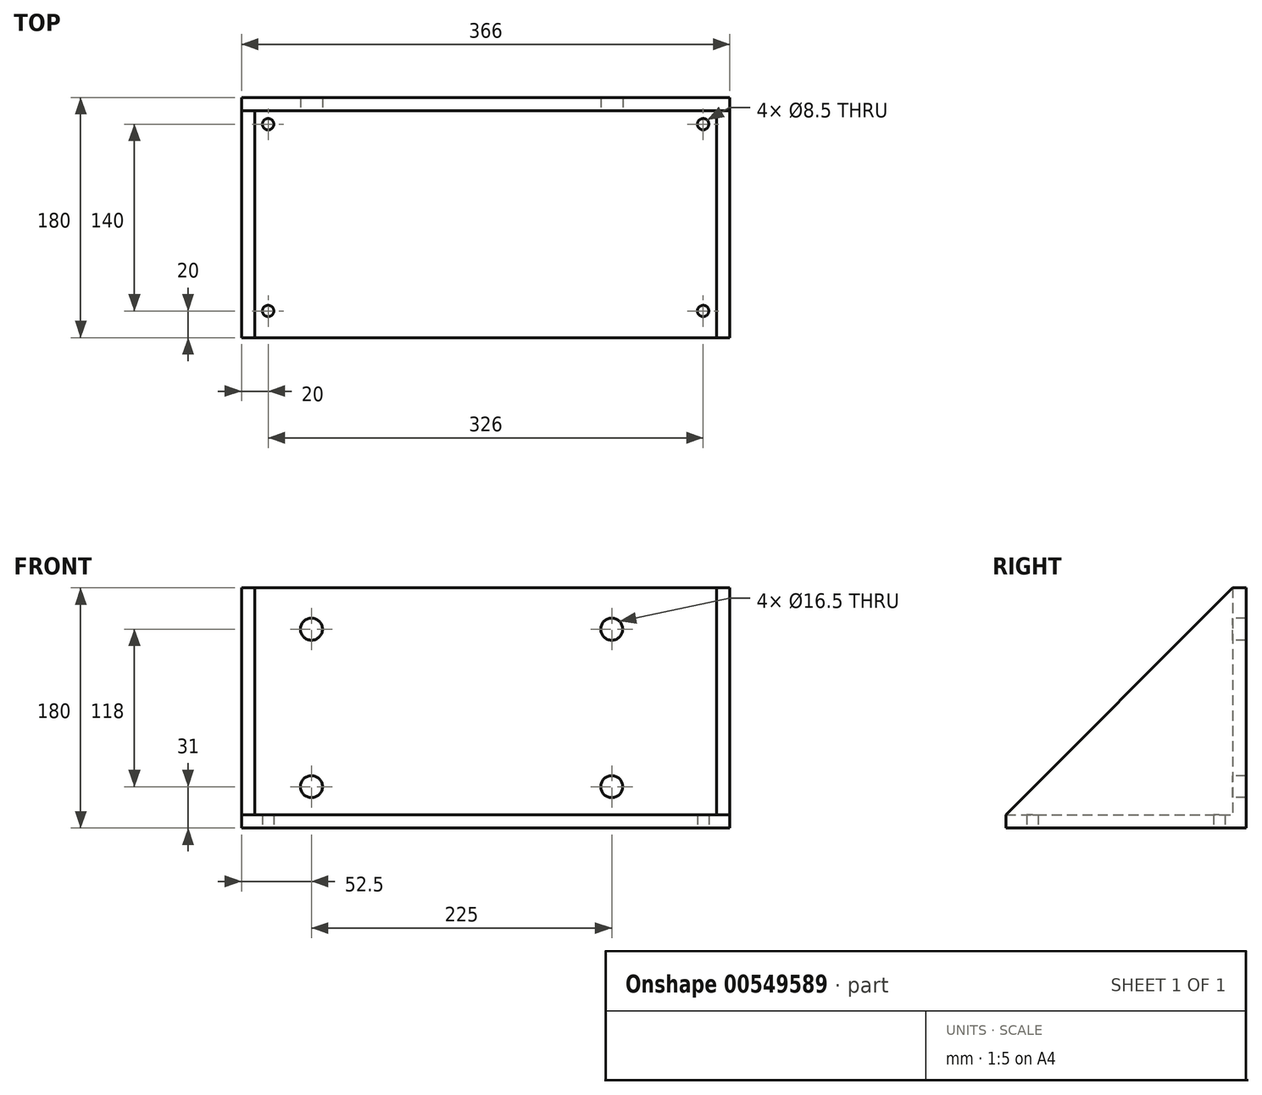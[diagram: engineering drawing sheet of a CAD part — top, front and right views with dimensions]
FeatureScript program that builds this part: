
annotation { "Feature Type Name" : "Feature", "Feature Type Description" : "" }
export const myFeature = defineFeature(function(context is Context, id is Id, definition is map)
    precondition{}
    {
        {
            var Q0;
            Q0=qCreatedBy(makeId("Right.planeOp"),FACE);
            var sketch = newSketch(context, id + "F0", { "sketchPlane" : qUnion([Q0])});
            skLineSegment(sketch, "E0", {"start": v(10, 85) * mm, "end": v(10, -95) * mm});
            skLineSegment(sketch, "E1", {"start": v(10, -95) * mm, "end": v(-170, -95) * mm});
            skLineSegment(sketch, "E2", {"start": v(-170, -95) * mm, "end": v(-170, -85) * mm});
            skLineSegment(sketch, "E3", {"start": v(-170, -85) * mm, "end": v(0, -85) * mm});
            skLineSegment(sketch, "E4", {"start": v(0, -85) * mm, "end": v(0, 85) * mm});
            skLineSegment(sketch, "E5", {"start": v(0, 85) * mm, "end": v(10, 85) * mm});
            skSolve(sketch);
        }
        {
            var Q0;
            Q0=makeQuery(id+"F0.imprint","IMPRINT",FACE,{"disambiguationData":[TD([[makeQuery(id+"F0.imprint","IMPRINT",EDGE,{"derivedFrom":sQuery(id+"F0.wireOp",EDGE,"E0")}),-1.0]])]});
            extrude(context, id + "F1", {"entities" : qUnion([Q0]), "depth" : 366 * mm, "offsetDistance" : 25 * mm});
        }
        {
            var Q0;
            Q0=makeQuery(id+"F1.opExtrude","SWEPT_FACE",FACE,{"disambiguationData":[OSD([sQuery(id+"F0.wireOp",EDGE,"E4")])]});
            var sketch = newSketch(context, id + "F2", { "sketchPlane" : qUnion([Q0])});
            skLineSegment(sketch, "E6", {"start": v(-34.72, 54) * mm, "end": v(411.3, 54) * mm, "construction": true});
            skLineSegment(sketch, "E7", {"start": v(-33.79, -64) * mm, "end": v(425.27, -64) * mm, "construction": true});
            skLineSegment(sketch, "E8", {"start": v(52.5, 122.85) * mm, "end": v(52.5, -132.75) * mm, "construction": true});
            skLineSegment(sketch, "E9", {"start": v(277.5, 121.45) * mm, "end": v(277.5, -137.87) * mm, "construction": true});
            skCircle(sketch, "E10", {"center": v(52.5, 54) * mm, "radius": 8.25 * mm});
            skCircle(sketch, "E11", {"center": v(277.5, -64) * mm, "radius": 8.25 * mm});
            skCircle(sketch, "E12", {"center": v(277.5, 54) * mm, "radius": 8.25 * mm});
            skCircle(sketch, "E13", {"center": v(52.5, -64) * mm, "radius": 8.25 * mm});
            skSolve(sketch);
        }
        {
            var Q0;
            Q0=makeQuery(id+"F2.imprint","IMPRINT",FACE,{"disambiguationData":[TD([[makeQuery(id+"F2.imprint","IMPRINT",EDGE,{"derivedFrom":sQuery(id+"F2.wireOp",EDGE,"E10")}),1.0]])]});
            var Q1;
            Q1=makeQuery(id+"F2.imprint","IMPRINT",FACE,{"disambiguationData":[TD([[makeQuery(id+"F2.imprint","IMPRINT",EDGE,{"derivedFrom":sQuery(id+"F2.wireOp",EDGE,"E12")}),1.0]])]});
            var Q2;
            Q2=makeQuery(id+"F2.imprint","IMPRINT",FACE,{"disambiguationData":[TD([[makeQuery(id+"F2.imprint","IMPRINT",EDGE,{"derivedFrom":sQuery(id+"F2.wireOp",EDGE,"E11")}),1.0]])]});
            var Q3;
            Q3=makeQuery(id+"F2.imprint","IMPRINT",FACE,{"disambiguationData":[TD([[makeQuery(id+"F2.imprint","IMPRINT",EDGE,{"derivedFrom":sQuery(id+"F2.wireOp",EDGE,"E13")}),1.0]])]});
            extrude(context, id + "F3", {"entities" : qUnion([Q0, Q1, Q2, Q3]), "operationType" : NewBodyOperationType.REMOVE, "endBound" : BoundingType.THROUGH_ALL, "oppositeDirection" : true, "depth" : 25 * mm, "offsetDistance" : 25 * mm});
        }
        {
            var Q0;
            Q0=makeQuery(id+"F1.opExtrude","SWEPT_FACE",FACE,{"disambiguationData":[OSD([sQuery(id+"F0.wireOp",EDGE,"E4")])]});
            var sketch = newSketch(context, id + "F4", { "sketchPlane" : qUnion([Q0])});
            skLineSegment(sketch, "E14.bottom", {"start": v(366, 85) * mm, "end": v(356, 85) * mm});
            skLineSegment(sketch, "E14.top", {"start": v(366, -85) * mm, "end": v(356, -85) * mm});
            skLineSegment(sketch, "E14.left", {"start": v(366, 85) * mm, "end": v(366, -85) * mm});
            skLineSegment(sketch, "E14.right", {"start": v(356, 85) * mm, "end": v(356, -85) * mm});
            skLineSegment(sketch, "E15.bottom", {"start": v(0, 85) * mm, "end": v(10, 85) * mm});
            skLineSegment(sketch, "E15.top", {"start": v(0, -85) * mm, "end": v(10, -85) * mm});
            skLineSegment(sketch, "E15.left", {"start": v(0, 85) * mm, "end": v(0, -85) * mm});
            skLineSegment(sketch, "E15.right", {"start": v(10, 85) * mm, "end": v(10, -85) * mm});
            skSolve(sketch);
        }
        {
            var Q0;
            Q0=makeQuery(id+"F4.imprint","IMPRINT",FACE,{"disambiguationData":[TD([[makeQuery(id+"F4.imprint","IMPRINT",EDGE,{"derivedFrom":sQuery(id+"F4.wireOp",EDGE,"E15.bottom")}),1.0]])]});
            var Q1;
            Q1=makeQuery(id+"F4.imprint","IMPRINT",FACE,{"disambiguationData":[TD([[makeQuery(id+"F4.imprint","IMPRINT",EDGE,{"derivedFrom":sQuery(id+"F4.wireOp",EDGE,"E14.bottom")}),1.0]])]});
            extrude(context, id + "F5", {"entities" : qUnion([Q0, Q1]), "operationType" : NewBodyOperationType.ADD, "depth" : 170 * mm, "offsetDistance" : 25 * mm});
        }
        {
            var Q0;
            Q0=makeQuery(id+"F5.boolean.opBoolean","MERGE",FACE,{"derivedFrom":[makeQuery(id+"F1.opExtrude","CAP_FACE",FACE,{"disambiguationData":[OSD([sQuery(id+"F0.wireOp",EDGE,"E0"),sQuery(id+"F0.wireOp",EDGE,"E1"),sQuery(id+"F0.wireOp",EDGE,"E2"),sQuery(id+"F0.wireOp",EDGE,"E3"),sQuery(id+"F0.wireOp",EDGE,"E4"),sQuery(id+"F0.wireOp",EDGE,"E5")])],"isStart":false}),makeQuery(id+"F5.opExtrude","SWEPT_FACE",FACE,{"disambiguationData":[OSD([sQuery(id+"F4.wireOp",EDGE,"E14.left")])]})]});
            var sketch = newSketch(context, id + "F6", { "sketchPlane" : qUnion([Q0])});
            skLineSegment(sketch, "E16", {"start": v(-225.43, -85) * mm, "end": v(49.68, -85) * mm, "construction": true});
            skLineSegment(sketch, "E17", {"start": v(5, 97.23) * mm, "end": v(5, -95) * mm, "construction": true});
            skLineSegment(sketch, "E18", {"start": v(5, 85) * mm, "end": v(-170, -85) * mm});
            skSolve(sketch);
        }
        {
            var Q0;
            Q0=makeQuery(id+"F5.boolean.opBoolean","MERGE",FACE,{"derivedFrom":[makeQuery(id+"F1.opExtrude","CAP_FACE",FACE,{"disambiguationData":[OSD([sQuery(id+"F0.wireOp",EDGE,"E0"),sQuery(id+"F0.wireOp",EDGE,"E1"),sQuery(id+"F0.wireOp",EDGE,"E2"),sQuery(id+"F0.wireOp",EDGE,"E3"),sQuery(id+"F0.wireOp",EDGE,"E4"),sQuery(id+"F0.wireOp",EDGE,"E5")])],"isStart":true}),makeQuery(id+"F5.opExtrude","SWEPT_FACE",FACE,{"disambiguationData":[OSD([sQuery(id+"F4.wireOp",EDGE,"E15.left")])]})]});
            var sketch = newSketch(context, id + "F7", { "sketchPlane" : qUnion([Q0])});
            skLineSegment(sketch, "E19", {"start": v(-23.48, -85) * mm, "end": v(187.5, -85) * mm, "construction": true});
            skLineSegment(sketch, "E20", {"start": v(0, 160.14) * mm, "end": v(0, -178.78) * mm, "construction": true});
            skLineSegment(sketch, "E21", {"start": v(0, 85) * mm, "end": v(170, -85) * mm});
            skSolve(sketch);
        }
        {
            var Q0;
            {var subQ0=sQuery(id+"F7.wireOp",EDGE,"E21");Q0=makeQuery(id+"F7.imprint","IMPRINT",FACE,{"disambiguationData":[TD([[makeQuery(id+"F7.imprint","IMPRINT",EDGE,{"derivedFrom":subQ0}),1.0]])]});}
            var Q1;
            {var subQ0=sQuery(id+"F6.wireOp",EDGE,"E18");Q1=makeQuery(id+"F6.imprint","IMPRINT",FACE,{"disambiguationData":[TD([[makeQuery(id+"F6.imprint","IMPRINT",EDGE,{"derivedFrom":subQ0}),-1.0]])]});}
            extrude(context, id + "F8", {"entities" : qUnion([Q0, Q1]), "operationType" : NewBodyOperationType.REMOVE, "endBound" : BoundingType.THROUGH_ALL, "oppositeDirection" : true, "depth" : 25 * mm, "offsetDistance" : 25 * mm});
        }
        {
            var Q0;
            Q0=makeQuery(id+"F1.opExtrude","SWEPT_FACE",FACE,{"disambiguationData":[OSD([sQuery(id+"F0.wireOp",EDGE,"E1")])]});
            var sketch = newSketch(context, id + "F9", { "sketchPlane" : qUnion([Q0])});
            skLineSegment(sketch, "E22.bottom", {"start": v(0, 30) * mm, "end": v(40, 30) * mm, "construction": true});
            skLineSegment(sketch, "E22.top", {"start": v(0, -10) * mm, "end": v(40, -10) * mm, "construction": true});
            skLineSegment(sketch, "E22.left", {"start": v(0, 30) * mm, "end": v(0, -10) * mm, "construction": true});
            skLineSegment(sketch, "E22.right", {"start": v(40, 30) * mm, "end": v(40, -10) * mm, "construction": true});
            skLineSegment(sketch, "E23.bottom", {"start": v(40, 170) * mm, "end": v(0, 170) * mm, "construction": true});
            skLineSegment(sketch, "E23.top", {"start": v(40, 130) * mm, "end": v(0, 130) * mm, "construction": true});
            skLineSegment(sketch, "E23.left", {"start": v(40, 170) * mm, "end": v(40, 130) * mm, "construction": true});
            skLineSegment(sketch, "E23.right", {"start": v(0, 170) * mm, "end": v(0, 130) * mm, "construction": true});
            skLineSegment(sketch, "E24.bottom", {"start": v(326, 170) * mm, "end": v(366, 170) * mm, "construction": true});
            skLineSegment(sketch, "E24.top", {"start": v(326, 130) * mm, "end": v(366, 130) * mm, "construction": true});
            skLineSegment(sketch, "E24.left", {"start": v(326, 170) * mm, "end": v(326, 130) * mm, "construction": true});
            skLineSegment(sketch, "E24.right", {"start": v(366, 170) * mm, "end": v(366, 130) * mm, "construction": true});
            skLineSegment(sketch, "E25.bottom", {"start": v(366, 30) * mm, "end": v(326, 30) * mm, "construction": true});
            skLineSegment(sketch, "E25.top", {"start": v(366, -10) * mm, "end": v(326, -10) * mm, "construction": true});
            skLineSegment(sketch, "E25.left", {"start": v(366, 30) * mm, "end": v(366, -10) * mm, "construction": true});
            skLineSegment(sketch, "E25.right", {"start": v(326, 30) * mm, "end": v(326, -10) * mm, "construction": true});
            skLineSegment(sketch, "E26", {"start": v(-48.92, 150) * mm, "end": v(452.17, 150) * mm, "construction": true});
            skLineSegment(sketch, "E27", {"start": v(478.38, 10) * mm, "end": v(-89.8, 10) * mm, "construction": true});
            skLineSegment(sketch, "E28", {"start": v(346, 230.4) * mm, "end": v(346, -90.39) * mm, "construction": true});
            skLineSegment(sketch, "E29", {"start": v(20, 224.2) * mm, "end": v(20, -106.05) * mm, "construction": true});
            skCircle(sketch, "E30", {"center": v(20, 150) * mm, "radius": 4.25 * mm});
            skCircle(sketch, "E31", {"center": v(346, 150) * mm, "radius": 4.25 * mm});
            skCircle(sketch, "E32", {"center": v(20, 10) * mm, "radius": 4.25 * mm});
            skCircle(sketch, "E33", {"center": v(346, 10) * mm, "radius": 4.25 * mm});
            skSolve(sketch);
        }
        {
            var Q0;
            Q0=makeQuery(id+"F9.imprint","IMPRINT",FACE,{"disambiguationData":[TD([[makeQuery(id+"F9.imprint","IMPRINT",EDGE,{"derivedFrom":sQuery(id+"F9.wireOp",EDGE,"E30")}),1.0]])]});
            var Q1;
            Q1=makeQuery(id+"F9.imprint","IMPRINT",FACE,{"disambiguationData":[TD([[makeQuery(id+"F9.imprint","IMPRINT",EDGE,{"derivedFrom":sQuery(id+"F9.wireOp",EDGE,"E32")}),1.0]])]});
            var Q2;
            Q2=makeQuery(id+"F9.imprint","IMPRINT",FACE,{"disambiguationData":[TD([[makeQuery(id+"F9.imprint","IMPRINT",EDGE,{"derivedFrom":sQuery(id+"F9.wireOp",EDGE,"E33")}),1.0]])]});
            var Q3;
            Q3=makeQuery(id+"F9.imprint","IMPRINT",FACE,{"disambiguationData":[TD([[makeQuery(id+"F9.imprint","IMPRINT",EDGE,{"derivedFrom":sQuery(id+"F9.wireOp",EDGE,"E31")}),1.0]])]});
            extrude(context, id + "F10", {"entities" : qUnion([Q0, Q1, Q2, Q3]), "operationType" : NewBodyOperationType.REMOVE, "endBound" : BoundingType.THROUGH_ALL, "oppositeDirection" : true, "depth" : 25 * mm, "offsetDistance" : 25 * mm});
        }
    });
